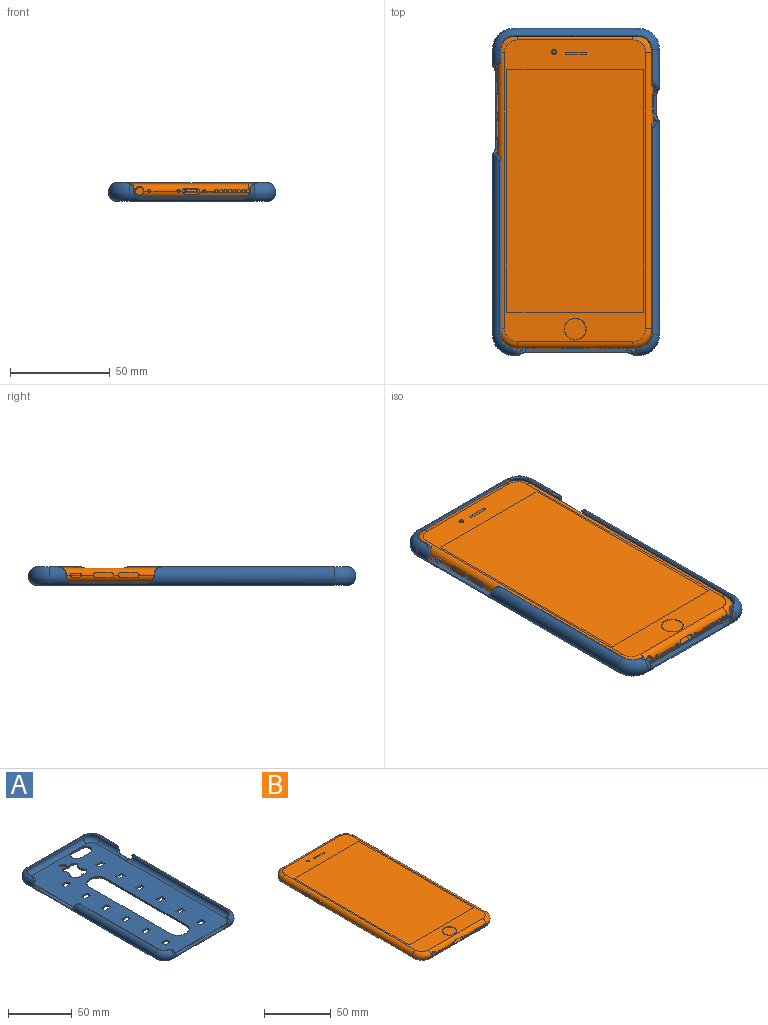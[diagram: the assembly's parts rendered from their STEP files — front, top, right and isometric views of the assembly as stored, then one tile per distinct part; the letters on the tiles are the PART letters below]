
ASSEMBLY  parts=2 mates=1
PART A: 155 faces, bbox 85.4x165.7x9.4 mm
  f0: plane 157.7x77.4mm, normal (0,0,-1), area 9656.5mm2, adj f6,f11,f14,f16,f19,f22,f25,f28
  f1: plane 153.78x73.54mm, normal (0,0,1), area 8760.7mm2, adj f2,f4,f7,f8,f12,f17,f20,f23
  f2: cylinder r=3.5mm len=142.7mm, axis (0,1,0), area 1310mm2, adj f1,f3,f17,f18,f20,f53,f54,f55
  f3: cylinder r=0.5mm len=105.58mm, axis (0,1,0), area 163.5mm2, adj f2,f10,f19,f59,f60
  f4: cylinder r=3.5mm len=142.7mm, axis (0,1,0), area 1033.7mm2, adj f1,f5,f7,f12,f26,f29,f30,f42
  f5: cylinder r=0.5mm len=6.96mm, axis (0,1,0), area 8.5mm2, adj f4,f6,f27,f46,f51
  f6: cylinder r=5mm len=142.7mm, axis (0,1,0), area 1290.4mm2, adj f0,f5,f14,f28,f29,f51,f52,f148
  f7: plane 11.88x0mm, normal (1,0,0), area 0mm2, adj f1,f4,f42
  f8: cylinder r=3.5mm len=62.4mm, axis (1,0,0), area 76.1mm2, adj f1,f9,f12,f15,f17,f31,f33,f34
  f9: cylinder r=0.5mm len=0.88mm, axis (1,0,0), area 0.3mm2, adj f8,f13,f38
  f10: torus R=6.88mm, axis (0,0,1), area 15.2mm2, adj f3,f11,f15,f17,f31,f32
  f11: torus R=5.6mm, axis (0,0,1), area 180.7mm2, adj f0,f10,f16,f19,f32,f140
  f12: torus R=5.74mm, axis (0,0,1), area 129.9mm2, adj f1,f4,f8,f13
  f13: torus R=6.88mm, axis (0,0,1), area 15.2mm2, adj f9,f12,f14,f29,f38,f39
  f14: torus R=5.6mm, axis (0,0,1), area 180.7mm2, adj f0,f6,f13,f16,f39,f132
  f15: cylinder r=0.5mm len=0.88mm, axis (1,0,0), area 0.3mm2, adj f8,f10,f31
  f16: cylinder r=5mm len=62.4mm, axis (1,0,0), area 162.3mm2, adj f0,f11,f14,f133,f134,f135,f136,f137
  f17: torus R=5.74mm, axis (0,0,1), area 129.9mm2, adj f1,f2,f8,f10
  f18: cylinder r=0.5mm len=18.28mm, axis (0,1,0), area 26.3mm2, adj f2,f19,f21,f53,f61
  f19: cylinder r=5mm len=142.7mm, axis (0,1,0), area 1579.2mm2, adj f0,f3,f11,f18,f22,f60,f61,f141
  f20: torus R=5.74mm, axis (0,0,1), area 129.9mm2, adj f1,f2,f21,f23
  f21: torus R=6.88mm, axis (0,0,1), area 16.2mm2, adj f18,f20,f22,f24
  f22: torus R=5.6mm, axis (0,0,1), area 182mm2, adj f0,f19,f21,f25
  f23: cylinder r=3.5mm len=62.4mm, axis (-1,0,0), area 638.1mm2, adj f1,f20,f24,f26
  f24: cylinder r=0.5mm len=62.4mm, axis (-1,0,0), area 98mm2, adj f21,f23,f25,f27
  f25: cylinder r=5mm len=62.4mm, axis (-1,0,0), area 767.6mm2, adj f0,f22,f24,f28
  f26: torus R=5.74mm, axis (0,0,1), area 129.9mm2, adj f1,f4,f23,f27
  f27: torus R=6.88mm, axis (0,0,1), area 16.2mm2, adj f5,f24,f26,f28
  f28: torus R=5.6mm, axis (0,0,1), area 182mm2, adj f0,f6,f25,f27
  f29: cylinder r=0.5mm len=88.94mm, axis (0,1,0), area 137.3mm2, adj f4,f6,f13,f47,f52
  f30: plane 93.82x0mm, normal (1,0,0), area 0.4mm2, adj f1,f4,f43
  f31: cylinder r=3.5mm len=3.87mm, axis (0,1,0), area 8.1mm2, adj f8,f10,f15,f32,f33,f139,f140
  f32: plane 1.41x0.34mm, normal (-1,0,0), area 0.2mm2, adj f10,f11,f31,f140
  f33: plane 1.07x0.54mm, normal (-1,0,0), area 0.5mm2, adj f8,f31,f34,f138
  f34: cylinder r=3.5mm len=4.36mm, axis (0,1,0), area 8.9mm2, adj f8,f33,f35,f137
  f35: plane 50.8x3.01mm, normal (0,0,1), area 152.9mm2, adj f8,f34,f36,f136
  f36: cylinder r=3.5mm len=4.36mm, axis (0,1,0), area 8.9mm2, adj f8,f35,f37,f135
  f37: plane 1.07x0.54mm, normal (1,0,0), area 0.5mm2, adj f8,f36,f38,f134
  f38: cylinder r=3.5mm len=3.87mm, axis (0,1,0), area 8.1mm2, adj f8,f9,f13,f37,f39,f132,f133
  f39: plane 1.41x0.34mm, normal (1,0,0), area 0.2mm2, adj f13,f14,f38,f132
  f40: cylinder r=3.5mm len=0.17mm, axis (0,1,0), area 0mm2, adj f1,f8
  f41: cylinder r=3.5mm len=0.17mm, axis (0,1,0), area 0mm2, adj f1,f8
  f42: cylinder r=3.5mm len=0.17mm, axis (-1,0,0), area 0mm2, adj f1,f4,f7
  f43: cylinder r=3.5mm len=0.17mm, axis (-1,0,0), area 0mm2, adj f1,f4,f30
  f44: plane 37x3.01mm, normal (0,0,1), area 111.4mm2, adj f4,f49,f50,f151
  f45: plane 1.07x0.54mm, normal (0,-1,0), area 0.5mm2, adj f4,f46,f49,f153
  f46: cylinder r=3.5mm len=3.76mm, axis (-1,0,0), area 8.4mm2, adj f4,f5,f45,f51,f154
  f47: cylinder r=3.5mm len=3.76mm, axis (-1,0,0), area 8.4mm2, adj f4,f29,f48,f52,f148
  f48: plane 1.1x1.04mm, normal (0,1,0), area 1.1mm2, adj f4,f47,f50,f149
  f49: cylinder r=3.5mm len=4.36mm, axis (-1,0,0), area 8.9mm2, adj f4,f44,f45,f152
  f50: cylinder r=3.5mm len=4.38mm, axis (-1,0,0), area 10.2mm2, adj f4,f44,f48,f150
  f51: plane 1.37x0.32mm, normal (0,-1,0), area 0.2mm2, adj f5,f6,f46,f154
  f52: plane 1.37x0.32mm, normal (0,1,0), area 0.2mm2, adj f6,f29,f47,f148
  f53: cylinder r=3.5mm len=3.76mm, axis (1,0,0), area 8.4mm2, adj f2,f18,f54,f61,f141
  f54: plane 1.07x0.54mm, normal (0,-1,0), area 0.5mm2, adj f2,f53,f55,f142
  f55: cylinder r=3.5mm len=4.36mm, axis (1,0,0), area 8.9mm2, adj f2,f54,f56,f143
  f56: plane 9x3.01mm, normal (0,0,1), area 27.1mm2, adj f2,f55,f57,f144
  f57: cylinder r=3.5mm len=4.36mm, axis (1,0,0), area 8.9mm2, adj f2,f56,f58,f145
  f58: plane 1.07x0.54mm, normal (0,1,0), area 0.5mm2, adj f2,f57,f59,f146
  f59: cylinder r=3.5mm len=3.76mm, axis (1,0,0), area 8.4mm2, adj f2,f3,f58,f60,f147
  f60: plane 1.37x0.32mm, normal (0,1,0), area 0.2mm2, adj f3,f19,f59,f147
  f61: plane 1.37x0.32mm, normal (0,-1,0), area 0.2mm2, adj f18,f19,f53,f141
  f62: cylinder r=3.5mm len=0.17mm, axis (1,0,0), area 0mm2, adj f1,f2
  f63: cylinder r=3.5mm len=0.17mm, axis (1,0,0), area 0mm2, adj f1,f2
  f64: plane 10.11x1.6mm, normal (0,-1,0), area 16.2mm2, adj f0,f1,f65,f67
  f65: cylinder r=5mm len=10mm, axis (0,0,1), area 25.1mm2, adj f0,f1,f64,f66
  f66: plane 10.11x1.6mm, normal (0,1,0), area 16.2mm2, adj f0,f1,f65,f67
  f67: cylinder r=5mm len=10mm, axis (0,0,1), area 25.1mm2, adj f0,f1,f64,f66
  f68: plane 5.7x1.6mm, normal (0,-1,0), area 9.1mm2, adj f0,f1,f69,f71
  f69: plane 4.7x1.6mm, normal (1,0,0), area 7.5mm2, adj f0,f1,f68,f70
  f70: plane 5.7x1.6mm, normal (0,1,0), area 9.1mm2, adj f0,f1,f69,f71
  f71: plane 4.7x1.6mm, normal (-1,0,0), area 7.5mm2, adj f0,f1,f68,f70
  f72: plane 6.2x1.6mm, normal (0,-1,0), area 9.9mm2, adj f0,f1,f73,f75
  f73: plane 4.2x1.6mm, normal (1,0,0), area 6.7mm2, adj f0,f1,f72,f74
  f74: plane 6.2x1.6mm, normal (0,1,0), area 9.9mm2, adj f0,f1,f73,f75
  f75: plane 4.2x1.6mm, normal (-1,0,0), area 6.7mm2, adj f0,f1,f72,f74
  f76: plane 4.2x1.6mm, normal (1,0,0), area 6.7mm2, adj f0,f1,f77,f79
  f77: plane 6.2x1.6mm, normal (0,1,0), area 9.9mm2, adj f0,f1,f76,f78
  f78: plane 4.2x1.6mm, normal (-1,0,0), area 6.7mm2, adj f0,f1,f77,f79
  f79: plane 6.2x1.6mm, normal (0,-1,0), area 9.9mm2, adj f0,f1,f76,f78
  f80: plane 4.2x1.6mm, normal (-1,0,0), area 6.7mm2, adj f0,f1,f81,f83
  f81: plane 6.2x1.6mm, normal (0,-1,0), area 9.9mm2, adj f0,f1,f80,f82
  f82: plane 4.2x1.6mm, normal (1,0,0), area 6.7mm2, adj f0,f1,f81,f83
  f83: plane 6.2x1.6mm, normal (0,1,0), area 9.9mm2, adj f0,f1,f80,f82
  f84: plane 1.6x1.4mm, normal (0,-1,0), area 2.2mm2, adj f0,f1,f85,f93
  f85: cylinder r=8mm len=8mm, axis (0,0,1), area 20.1mm2, adj f0,f1,f84,f86
  f86: plane 15.56x1.6mm, normal (1,0,0), area 24.9mm2, adj f0,f1,f85,f87
  f87: plane 73.97x1.6mm, normal (1,0,0), area 118.4mm2, adj f0,f1,f86,f88
  f88: cylinder r=8mm len=8mm, axis (0,0,1), area 20.1mm2, adj f0,f1,f87,f89
  f89: plane 1.6x1.4mm, normal (0,1,0), area 2.2mm2, adj f0,f1,f88,f90
  f90: cylinder r=8mm len=8mm, axis (0,0,1), area 20.1mm2, adj f0,f1,f89,f91
  f91: plane 73.97x1.6mm, normal (-1,0,0), area 118.4mm2, adj f0,f1,f90,f92
  f92: plane 15.56x1.6mm, normal (-1,0,0), area 24.9mm2, adj f0,f1,f91,f93
  f93: cylinder r=8mm len=8mm, axis (0,0,1), area 20.1mm2, adj f0,f1,f84,f92
  f94: cylinder r=6.86mm len=10.84mm, axis (0,0,1), area 20.1mm2, adj f0,f1,f95,f97
  f95: extruded ~16.45x2.52mm, area 29.2mm2, adj f0,f1,f94,f96
  f96: extruded ~8.84x3.05mm, area 17.5mm2, adj f0,f1,f95,f97
  f97: extruded ~16.31x5.97mm, area 34.2mm2, adj f0,f1,f94,f96
  f98: extruded ~5.13x4.51mm, area 12.3mm2, adj f0,f1,f99
  f99: extruded ~5.12x4.51mm, area 12mm2, adj f0,f1,f98
  f100: plane 6.2x1.6mm, normal (0,-1,0), area 9.9mm2, adj f0,f1,f101,f103
  f101: plane 4.2x1.6mm, normal (1,0,0), area 6.7mm2, adj f0,f1,f100,f102
  f102: plane 6.2x1.6mm, normal (0,1,0), area 9.9mm2, adj f0,f1,f101,f103
  f103: plane 4.2x1.6mm, normal (-1,0,0), area 6.7mm2, adj f0,f1,f100,f102
  f104: plane 5.7x1.6mm, normal (0,-1,0), area 9.1mm2, adj f0,f1,f105,f107
  f105: plane 4.7x1.6mm, normal (1,0,0), area 7.5mm2, adj f0,f1,f104,f106
  f106: plane 5.7x1.6mm, normal (0,1,0), area 9.1mm2, adj f0,f1,f105,f107
  f107: plane 4.7x1.6mm, normal (-1,0,0), area 7.5mm2, adj f0,f1,f104,f106
  f108: plane 6.2x1.6mm, normal (0,-1,0), area 9.9mm2, adj f0,f1,f109,f111
  f109: plane 4.2x1.6mm, normal (1,0,0), area 6.7mm2, adj f0,f1,f108,f110
  f110: plane 6.2x1.6mm, normal (0,1,0), area 9.9mm2, adj f0,f1,f109,f111
  f111: plane 4.2x1.6mm, normal (-1,0,0), area 6.7mm2, adj f0,f1,f108,f110
  f112: plane 6.2x1.6mm, normal (0,-1,0), area 9.9mm2, adj f0,f1,f113,f115
  f113: plane 4.2x1.6mm, normal (1,0,0), area 6.7mm2, adj f0,f1,f112,f114
  f114: plane 6.2x1.6mm, normal (0,1,0), area 9.9mm2, adj f0,f1,f113,f115
  f115: plane 4.2x1.6mm, normal (-1,0,0), area 6.7mm2, adj f0,f1,f112,f114
  f116: plane 6.2x1.6mm, normal (0,-1,0), area 9.9mm2, adj f0,f1,f117,f119
  f117: plane 4.2x1.6mm, normal (1,0,0), area 6.7mm2, adj f0,f1,f116,f118
  f118: plane 6.2x1.6mm, normal (0,1,0), area 9.9mm2, adj f0,f1,f117,f119
  f119: plane 4.2x1.6mm, normal (-1,0,0), area 6.7mm2, adj f0,f1,f116,f118
  f120: plane 6.2x1.6mm, normal (0,-1,0), area 9.9mm2, adj f0,f1,f121,f123
  f121: plane 4.2x1.6mm, normal (1,0,0), area 6.7mm2, adj f0,f1,f120,f122
  f122: plane 6.2x1.6mm, normal (0,1,0), area 9.9mm2, adj f0,f1,f121,f123
  f123: plane 4.2x1.6mm, normal (-1,0,0), area 6.7mm2, adj f0,f1,f120,f122
  f124: plane 6.2x1.6mm, normal (0,-1,0), area 9.9mm2, adj f0,f1,f125,f127
  f125: plane 4.2x1.6mm, normal (1,0,0), area 6.7mm2, adj f0,f1,f124,f126
  f126: plane 6.2x1.6mm, normal (0,1,0), area 9.9mm2, adj f0,f1,f125,f127
  f127: plane 4.2x1.6mm, normal (-1,0,0), area 6.7mm2, adj f0,f1,f124,f126
  f128: plane 6.2x1.6mm, normal (0,-1,0), area 9.9mm2, adj f0,f1,f129,f131
  f129: plane 4.2x1.6mm, normal (1,0,0), area 6.7mm2, adj f0,f1,f128,f130
  f130: plane 6.2x1.6mm, normal (0,1,0), area 9.9mm2, adj f0,f1,f129,f131
  f131: plane 4.2x1.6mm, normal (-1,0,0), area 6.7mm2, adj f0,f1,f128,f130
  f132: bspline ~1.33x0.67mm, area 0.2mm2, adj f14,f38,f39,f133
  f133: bspline ~3.25x2.39mm, area 1.5mm2, adj f16,f38,f132,f134
  f134: cone r=4.7mm half-angle=45deg, axis (-1,0,0), area 0.2mm2, adj f16,f37,f133,f135
  f135: bspline ~4.04x3.8mm, area 2.9mm2, adj f16,f36,f134,f136
  f136: plane 50.8x0.51mm, normal (0,-0.92,0.38), area 28mm2, adj f16,f35,f135,f137
  f137: bspline ~4.04x3.8mm, area 2.9mm2, adj f16,f34,f136,f138
  f138: cone r=5mm half-angle=45deg, axis (1,0,0), area 0.2mm2, adj f16,f33,f137,f139
  f139: bspline ~3.25x2.39mm, area 1.5mm2, adj f16,f31,f138,f140
  f140: bspline ~1.4x0.68mm, area 0.2mm2, adj f11,f31,f32,f139
  f141: bspline ~3.81x3.54mm, area 1.7mm2, adj f19,f53,f61,f142
  f142: cone r=4.7mm half-angle=45deg, axis (0,1,0), area 0.2mm2, adj f19,f54,f141,f143
  f143: bspline ~4.04x3.8mm, area 2.9mm2, adj f19,f55,f142,f144
  f144: plane 9x0.51mm, normal (0.92,0,0.38), area 5mm2, adj f19,f56,f143,f145
  f145: bspline ~4.04x3.8mm, area 2.9mm2, adj f19,f57,f144,f146
  f146: cone r=4.7mm half-angle=45deg, axis (0,-1,0), area 0.2mm2, adj f19,f58,f145,f147
  f147: bspline ~3.81x3.54mm, area 1.7mm2, adj f19,f59,f60,f146
  f148: bspline ~3.81x3.54mm, area 1.7mm2, adj f6,f47,f52,f149
  f149: cone r=5mm half-angle=45deg, axis (0,-1,0), area 0.5mm2, adj f6,f48,f148,f150
  f150: bspline ~3.76x3.53mm, area 2.7mm2, adj f6,f50,f149,f151
  f151: plane 37x0.51mm, normal (-0.92,0,0.38), area 20.4mm2, adj f6,f44,f150,f152
  f152: bspline ~4.04x3.8mm, area 2.9mm2, adj f6,f49,f151,f153
  f153: cone r=5mm half-angle=45deg, axis (0,1,0), area 0.2mm2, adj f6,f45,f152,f154
  f154: bspline ~3.81x3.54mm, area 1.7mm2, adj f6,f46,f51,f153
PART B: 184 faces, bbox 79.4x159.7x7.8 mm
  f0: cylinder r=3.55mm len=3.55mm, axis (0,1,0), area 12.2mm2, adj f2,f5,f6,f32,f62
  f1: cylinder r=3.55mm len=3.55mm, axis (0,-1,0), area 12.2mm2, adj f2,f4,f7,f36,f59
  f2: plane 70.69x1.5mm, normal (0,0,-1), area 106mm2, adj f0,f1,f8,f39
  f3: cylinder r=3.55mm len=57.79mm, axis (-1,0,0), area 154.9mm2, adj f4,f5,f9,f10,f11,f12,f13,f14
  f4: torus R=6.45mm, axis (0,0,-1), area 41.5mm2, adj f1,f3,f22,f23,f49,f50
  f5: torus R=6.45mm, axis (0,0,-1), area 42.1mm2, adj f0,f3,f24,f25,f69
  f6: cylinder r=3.55mm len=132.83mm, axis (0,1,0), area 710.8mm2, adj f0,f8,f28,f62,f78,f79,f81,f83
  f7: cylinder r=3.55mm len=132.83mm, axis (0,-1,0), area 709.9mm2, adj f1,f8,f27,f59,f74,f99,f100,f101
  f8: plane 132.83x70.69mm, normal (0,0,-1), area 9132.5mm2, adj f2,f6,f7,f26,f48,f65
  f9: cylinder r=3.55mm len=0.95mm, axis (-1,0,0), area 0.1mm2, adj f3,f43,f148
  f10: cylinder r=3.55mm len=2mm, axis (-1,0,0), area 0.4mm2, adj f3,f43,f56,f148
  f11: cylinder r=3.55mm len=13.09mm, axis (-1,0,0), area 4.2mm2, adj f3,f40,f43,f56
  f12: cylinder r=3.55mm len=1.41mm, axis (-1,0,0), area 0.5mm2, adj f3,f40,f43,f109
  f13: cylinder r=3.55mm len=1.49mm, axis (-1,0,0), area 0.7mm2, adj f3,f43,f44,f111
  f14: cylinder r=3.55mm len=5.01mm, axis (-1,0,0), area 2.5mm2, adj f3,f43,f44,f131
  f15: cylinder r=3.55mm len=1.06mm, axis (-1,0,0), area 0.5mm2, adj f3,f43,f129,f131
  f16: cylinder r=3.55mm len=1.09mm, axis (-1,0,0), area 0.5mm2, adj f3,f43,f127,f129
  f17: cylinder r=3.55mm len=1.12mm, axis (-1,0,0), area 0.5mm2, adj f3,f43,f125,f127
  f18: cylinder r=3.55mm len=1.14mm, axis (-1,0,0), area 0.5mm2, adj f3,f43,f123,f125
  f19: cylinder r=3.55mm len=1.17mm, axis (-1,0,0), area 0.5mm2, adj f3,f43,f121,f123
  f20: cylinder r=3.55mm len=1.2mm, axis (-1,0,0), area 0.6mm2, adj f3,f43,f119,f121
  f21: cylinder r=3.55mm len=1.23mm, axis (-1,0,0), area 0.6mm2, adj f3,f43,f117,f119
  f22: torus R=6.45mm, axis (0,0,-1), area 4.3mm2, adj f4,f50
  f23: torus R=6.45mm, axis (0,0,-1), area 5.8mm2, adj f4,f50,f117
  f24: torus R=6.45mm, axis (0,0,-1), area 4.7mm2, adj f5,f72
  f25: torus R=6.45mm, axis (0,0,-1), area 4.7mm2, adj f5,f72
  f26: plane 70.69x1.5mm, normal (0,0,-1), area 106mm2, adj f8,f27,f28,f47
  f27: cylinder r=3.55mm len=3.55mm, axis (0,-1,0), area 12.2mm2, adj f7,f26,f31,f58,f59
  f28: cylinder r=3.55mm len=3.55mm, axis (0,1,0), area 12.1mm2, adj f6,f26,f29,f33,f61,f62
  f29: torus R=6.45mm, axis (0,0,-1), area 42.4mm2, adj f28,f30,f34,f35,f66,f67
  f30: cylinder r=3.55mm len=57.79mm, axis (1,0,0), area 196mm2, adj f29,f31,f68,f70
  f31: torus R=6.45mm, axis (0,0,-1), area 42.1mm2, adj f27,f30,f37,f38,f71
  f32: cylinder r=3.55mm len=2.05mm, axis (0,1,0), area 2.4mm2, adj f0,f39,f69
  f33: cylinder r=3.55mm len=0.28mm, axis (0,1,0), area 0mm2, adj f28,f34,f62
  f34: torus R=6.45mm, axis (0,0,-1), area 3.4mm2, adj f29,f33,f67
  f35: torus R=6.45mm, axis (0,0,-1), area 5.7mm2, adj f29,f67
  f36: cylinder r=3.55mm len=2.05mm, axis (0,-1,0), area 2.4mm2, adj f1,f39,f49
  f37: torus R=6.45mm, axis (0,0,-1), area 4.7mm2, adj f31,f73
  f38: torus R=6.45mm, axis (0,0,-1), area 4.7mm2, adj f31,f73
  f39: plane 70.69x7.57mm, normal (0,0,-1), area 517.3mm2, adj f2,f32,f36,f42,f49,f69
  f40: cylinder r=3.55mm len=1.6mm, axis (-1,0,0), area 0.8mm2, adj f3,f11,f12,f41,f168,f169,f170,f171
  f41: cylinder r=3.55mm len=1.6mm, axis (1,0,0), area 0.9mm2, adj f40,f43,f163,f164,f165,f166,f167,f168
  f42: cylinder r=3.55mm len=57.79mm, axis (-1,0,0), area 124.3mm2, adj f3,f39,f49,f69
  f43: cylinder r=3.55mm len=57.79mm, axis (1,0,0), area 290.7mm2, adj f9,f10,f11,f12,f13,f14,f15,f16
  f44: cylinder r=3.55mm len=1.6mm, axis (-1,0,0), area 0.8mm2, adj f3,f13,f14,f45,f153,f154,f155,f156
  f45: cylinder r=3.55mm len=1.6mm, axis (1,0,0), area 0.9mm2, adj f43,f44,f150,f151,f152,f153,f159,f160
  f46: plane 1.5x1.5mm, normal (0,0,1), area 1mm2, adj f142,f143
  f47: plane 70.69x7.57mm, normal (0,0,-1), area 456.1mm2, adj f26,f58,f61,f66,f68,f71,f104,f144
  f48: plane 18.21x17.51mm, normal (0,0,-1), area 242.8mm2, adj f8
  f49: torus R=6.45mm, axis (0,0,-1), area 24.6mm2, adj f4,f36,f39,f42
  f50: torus R=6.45mm, axis (0,0,-1), area 76.2mm2, adj f4,f22,f23,f43,f59,f63,f117
  f51: cylinder r=1.7mm len=1.7mm, axis (0,0,-1), area 1.5mm2, adj f52,f54,f113
  f52: cylinder r=1.7mm len=6.5mm, axis (1,0,0), area 10.1mm2, adj f51,f53,f54,f114
  f53: cylinder r=1.7mm len=1.7mm, axis (0,0,1), area 1.5mm2, adj f52,f54,f115
  f54: cylinder r=1.7mm len=6.5mm, axis (-1,0,0), area 10.1mm2, adj f51,f52,f53,f116
  f55: plane 8.7x2.95mm, normal (0,-1,0), area 12.7mm2, adj f109,f110,f111,f112,f113,f114,f115,f116
  f56: cylinder r=3.55mm len=1.6mm, axis (-1,0,0), area 1mm2, adj f3,f10,f11,f57
  f57: cylinder r=3.55mm len=1.6mm, axis (1,0,0), area 1mm2, adj f43,f56
  f58: cylinder r=3.55mm len=2.05mm, axis (0,-1,0), area 2.4mm2, adj f27,f47,f71
  f59: cylinder r=3.55mm len=138.07mm, axis (0,1,0), area 739.1mm2, adj f1,f7,f27,f50,f63,f73,f75,f98
  f60: plane 5.61x1.96mm, normal (-1,0,0), area 5.5mm2, adj f88,f89,f90,f91,f92,f93,f94,f95
  f61: cylinder r=3.55mm len=2.09mm, axis (0,1,0), area 2.5mm2, adj f28,f47,f66
  f62: cylinder r=3.55mm len=138.07mm, axis (0,-1,0), area 737.2mm2, adj f0,f6,f28,f33,f63,f67,f72,f79
  f63: plane 150.97x70.69mm, normal (0,0,1), area 2217.1mm2, adj f43,f50,f59,f62,f64,f67,f70,f72
  f64: plane 121.54x68.36mm, normal (0,0,1), area 8308.5mm2, adj f63
  f65: plane 5.18x4.88mm, normal (0,0,-1), area 13.6mm2, adj f8
  f66: torus R=6.45mm, axis (0,0,-1), area 24.8mm2, adj f29,f47,f61,f68
  f67: torus R=6.45mm, axis (0,0,-1), area 76.3mm2, adj f29,f34,f35,f62,f63,f70
  f68: cylinder r=3.55mm len=57.79mm, axis (1,0,0), area 126.3mm2, adj f30,f47,f66,f71,f106
  f69: torus R=6.45mm, axis (0,0,-1), area 24.8mm2, adj f5,f32,f39,f42
  f70: cylinder r=3.55mm len=57.79mm, axis (-1,0,0), area 322.3mm2, adj f30,f63,f67,f73
  f71: torus R=6.45mm, axis (0,0,-1), area 24.8mm2, adj f31,f47,f58,f68
  f72: torus R=6.45mm, axis (0,0,-1), area 76.3mm2, adj f24,f25,f43,f62,f63
  f73: torus R=6.45mm, axis (0,0,-1), area 76.3mm2, adj f37,f38,f59,f63,f70
  f74: cylinder r=3.55mm len=15.81mm, axis (0,-1,0), area 17.2mm2, adj f7,f75,f102
  f75: cylinder r=3.55mm len=15.81mm, axis (0,1,0), area 16.6mm2, adj f59,f74,f102
  f76: cone r=5.45mm half-angle=45deg, axis (0,0,1), area 7.2mm2, adj f63,f77
  f77: plane 10.6x10.6mm, normal (0,0,1), area 88.2mm2, adj f76
  f78: plane 7.4x0.59mm, normal (0,0,-1), area 4.3mm2, adj f6,f79,f81,f82
  f79: cylinder r=1.4mm len=2.8mm, axis (-1,0,0), area 2mm2, adj f6,f62,f78,f80,f82
  f80: plane 7.4x0.59mm, normal (0,0,1), area 4.3mm2, adj f62,f79,f81,f82
  f81: cylinder r=1.4mm len=2.8mm, axis (-1,0,0), area 2mm2, adj f6,f62,f78,f80,f82
  f82: plane 10.2x2.8mm, normal (-1,0,0), area 26.9mm2, adj f78,f79,f80,f81
  f83: plane 7.4x0.59mm, normal (0,0,-1), area 4.3mm2, adj f6,f84,f86,f87
  f84: cylinder r=1.4mm len=2.8mm, axis (-1,0,0), area 2mm2, adj f6,f62,f83,f85,f87
  f85: plane 7.4x0.59mm, normal (0,0,1), area 4.3mm2, adj f62,f84,f86,f87
  f86: cylinder r=1.4mm len=2.8mm, axis (-1,0,0), area 2mm2, adj f6,f62,f83,f85,f87
  f87: plane 10.2x2.8mm, normal (-1,0,0), area 26.9mm2, adj f83,f84,f85,f86
  f88: cylinder r=0.98mm len=1.96mm, axis (-1,0,0), area 1.3mm2, adj f6,f60,f62,f89,f91
  f89: plane 3.65x0.36mm, normal (0,0,-1), area 1.3mm2, adj f60,f62,f88,f90
  f90: cylinder r=0.98mm len=1.96mm, axis (-1,0,0), area 1.3mm2, adj f6,f60,f62,f89,f91
  f91: plane 3.65x0.36mm, normal (0,0,1), area 1.3mm2, adj f6,f60,f88,f90
  f92: cylinder r=0.47mm len=0.93mm, axis (1,0,0), area 1.2mm2, adj f60,f93,f95,f96
  f93: plane 4.31x0.8mm, normal (0,0,-1), area 3.4mm2, adj f60,f92,f94,f96
  f94: cylinder r=0.47mm len=0.93mm, axis (1,0,0), area 1.2mm2, adj f60,f93,f95,f96
  f95: plane 4.31x0.8mm, normal (0,0,1), area 3.4mm2, adj f60,f92,f94,f96
  f96: plane 5.24x0.93mm, normal (-1,0,0), area 4.7mm2, adj f92,f93,f94,f95
  f97: plane 10.2x2.8mm, normal (1,0,0), area 26.9mm2, adj f98,f99,f100,f101
  f98: plane 7.4x0.59mm, normal (0,0,1), area 4.3mm2, adj f59,f97,f99,f101
  f99: cylinder r=1.4mm len=2.8mm, axis (1,0,0), area 2mm2, adj f7,f59,f97,f98,f100
  f100: plane 7.4x0.59mm, normal (0,0,-1), area 4.3mm2, adj f7,f97,f99,f101
  f101: cylinder r=1.4mm len=2.8mm, axis (1,0,0), area 2mm2, adj f7,f59,f97,f98,f100
  f102: cylinder r=1mm len=2mm, axis (1,0,0), area 7.3mm2, adj f74,f75,f103
  f103: plane 2x2mm, normal (1,0,0), area 3.1mm2, adj f102
  f104: cylinder r=3.83mm len=7.66mm, axis (0,0,1), area 16.1mm2, adj f47,f105,f106
  f105: plane 7.66x7.66mm, normal (0,0,-1), area 46.1mm2, adj f104
  f106: plane 2.32x0.18mm, normal (0,0,1), area 0.3mm2, adj f68,f104
  f107: cylinder r=2.02mm len=9.64mm, axis (0,-1,0), area 117.8mm2, adj f108,f148,f149
  f108: plane 4.05x4.05mm, normal (0,-1,0), area 12.9mm2, adj f107
  f109: cylinder r=1.47mm len=5mm, axis (0,-1,0), area 22.5mm2, adj f3,f12,f43,f55,f110,f112
  f110: plane 5.75x4.68mm, normal (0,0,-1), area 26.9mm2, adj f43,f55,f109,f111
  f111: cylinder r=1.47mm len=5mm, axis (0,-1,0), area 22.5mm2, adj f3,f13,f43,f55,f110,f112
  f112: plane 5.75x4.68mm, normal (0,0,1), area 26.9mm2, adj f3,f55,f109,f111
  f113: plane 1.7x0.8mm, normal (1,0,0), area 1.4mm2, adj f51,f55,f114,f116
  f114: plane 6.5x0.8mm, normal (0,0,1), area 5.2mm2, adj f52,f55,f113,f115
  f115: plane 1.7x0.8mm, normal (-1,0,0), area 1.4mm2, adj f53,f55,f114,f116
  f116: plane 6.5x0.8mm, normal (0,0,-1), area 5.2mm2, adj f54,f55,f113,f115
  f117: cylinder r=0.8mm len=1.6mm, axis (0,-1,0), area 4.9mm2, adj f3,f21,f23,f43,f50,f118
  f118: plane 1.6x1.6mm, normal (0,-1,0), area 2mm2, adj f117
  f119: cylinder r=0.8mm len=1.6mm, axis (0,-1,0), area 4.9mm2, adj f3,f20,f21,f43,f120
  f120: plane 1.6x1.6mm, normal (0,-1,0), area 2mm2, adj f119
  f121: cylinder r=0.8mm len=1.6mm, axis (0,-1,0), area 4.9mm2, adj f3,f19,f20,f43,f122
  f122: plane 1.6x1.6mm, normal (0,-1,0), area 2mm2, adj f121
  f123: cylinder r=0.8mm len=1.6mm, axis (0,-1,0), area 4.9mm2, adj f3,f18,f19,f43,f124
  f124: plane 1.6x1.6mm, normal (0,-1,0), area 2mm2, adj f123
  f125: cylinder r=0.8mm len=1.6mm, axis (0,-1,0), area 4.9mm2, adj f3,f17,f18,f43,f126
  f126: plane 1.6x1.6mm, normal (0,-1,0), area 2mm2, adj f125
  f127: cylinder r=0.8mm len=1.6mm, axis (0,-1,0), area 4.9mm2, adj f3,f16,f17,f43,f128
  f128: plane 1.6x1.6mm, normal (0,-1,0), area 2mm2, adj f127
  f129: cylinder r=0.8mm len=1.6mm, axis (0,-1,0), area 4.9mm2, adj f3,f15,f16,f43,f130
  f130: plane 1.6x1.6mm, normal (0,-1,0), area 2mm2, adj f129
  f131: cylinder r=0.8mm len=1.6mm, axis (0,-1,0), area 4.9mm2, adj f3,f14,f15,f43,f132
  f132: plane 1.6x1.6mm, normal (0,-1,0), area 2mm2, adj f131
  f133: cylinder r=0.6mm len=1.2mm, axis (0,0,1), area 0.2mm2, adj f63,f134,f136,f137
  f134: plane 9.5x0.1mm, normal (0,-1,0), area 1mm2, adj f63,f133,f135,f137
  f135: cylinder r=0.6mm len=1.2mm, axis (0,0,1), area 0.2mm2, adj f63,f134,f136,f137
  f136: plane 9.5x0.1mm, normal (0,1,0), area 1mm2, adj f63,f133,f135,f137
  f137: plane 10.7x1.2mm, normal (0,0,1), area 12.5mm2, adj f133,f134,f135,f136
  f138: cylinder r=1.25mm len=2.5mm, axis (0,0,1), area 2mm2, adj f63,f139
  f139: plane 2.5x2.5mm, normal (0,0,1), area 1.8mm2, adj f138,f140
  f140: cylinder r=1mm len=2mm, axis (0,0,1), area 1.6mm2, adj f139,f141
  f141: plane 2x2mm, normal (0,0,1), area 1.4mm2, adj f140,f142
  f142: cylinder r=0.75mm len=1.5mm, axis (0,0,1), area 1.2mm2, adj f46,f141
  f143: sphere r=0.5mm, area 1.6mm2, adj f46
  f144: cylinder r=2.06mm len=4.11mm, axis (0,0,1), area 0.6mm2, adj f47,f145
  f145: plane 4.11x4.11mm, normal (0,0,-1), area 13.3mm2, adj f144
  f146: cylinder r=0.8mm len=1.6mm, axis (0,0,-1), area 0.5mm2, adj f47,f147
  f147: plane 1.6x1.6mm, normal (0,0,-1), area 2mm2, adj f146
  f148: bspline ~4.23x2.35mm, area 2.8mm2, adj f3,f9,f10,f107,f149
  f149: bspline ~4.23x2.35mm, area 2.8mm2, adj f43,f107,f148
  f150: plane 0.2x0.17mm, normal (0,0,-1), area 0mm2, adj f45,f151,f161,f162
  f151: plane 0.35x0.2mm, normal (-1,0,0), area 0.1mm2, adj f45,f150,f152,f162
  f152: plane 0.35x0.2mm, normal (0,0,-1), area 0.1mm2, adj f45,f151,f153,f162
  f153: plane 0.2x0.2mm, normal (-1,0,0), area 0mm2, adj f44,f45,f152,f154,f162
  f154: plane 0.35x0.2mm, normal (0,0,1), area 0.1mm2, adj f44,f153,f155,f162
  f155: plane 0.35x0.2mm, normal (-1,0,0), area 0.1mm2, adj f44,f154,f156,f162
  f156: plane 0.2x0.17mm, normal (0,0,1), area 0mm2, adj f44,f155,f157,f162
  f157: plane 0.35x0.2mm, normal (1,0,0), area 0.1mm2, adj f44,f156,f158,f162
  f158: plane 0.35x0.2mm, normal (0,0,1), area 0.1mm2, adj f44,f157,f159,f162
  f159: plane 0.2x0.2mm, normal (1,0,0), area 0mm2, adj f44,f45,f158,f160,f162
  f160: plane 0.35x0.2mm, normal (0,0,-1), area 0.1mm2, adj f45,f159,f161,f162
  f161: plane 0.35x0.2mm, normal (1,0,0), area 0.1mm2, adj f45,f150,f160,f162
  f162: plane 0.9x0.9mm, normal (0,-1,0), area 0.3mm2, adj f150,f151,f152,f153,f154,f155,f156,f157
  f163: plane 0.35x0.2mm, normal (0,0,-1), area 0.1mm2, adj f41,f164,f174,f175
  f164: plane 0.35x0.2mm, normal (-1,0,0), area 0.1mm2, adj f41,f163,f165,f175
  f165: plane 0.2x0.17mm, normal (0,0,-1), area 0mm2, adj f41,f164,f166,f175
  f166: plane 0.35x0.2mm, normal (1,0,0), area 0.1mm2, adj f41,f165,f167,f175
  f167: plane 0.35x0.2mm, normal (0,0,-1), area 0.1mm2, adj f41,f166,f168,f175
  f168: plane 0.2x0.2mm, normal (1,0,0), area 0mm2, adj f40,f41,f167,f169,f175
  f169: plane 0.35x0.2mm, normal (0,0,1), area 0.1mm2, adj f40,f168,f170,f175
  f170: plane 0.35x0.2mm, normal (1,0,0), area 0.1mm2, adj f40,f169,f171,f175
  f171: plane 0.2x0.17mm, normal (0,0,1), area 0mm2, adj f40,f170,f172,f175
  f172: plane 0.35x0.2mm, normal (-1,0,0), area 0.1mm2, adj f40,f171,f173,f175
  f173: plane 0.35x0.2mm, normal (0,0,1), area 0.1mm2, adj f40,f172,f174,f175
  f174: plane 0.2x0.2mm, normal (-1,0,0), area 0mm2, adj f40,f41,f163,f173,f175
  f175: plane 0.9x0.9mm, normal (0,-1,0), area 0.3mm2, adj f163,f164,f165,f166,f167,f168,f169,f170
  f176: plane 6.9x6.9mm, normal (0,0,1), area 37.4mm2, adj f183
  f177: sphere r=1.52mm, area 4.8mm2, adj f178
  f178: cylinder r=1.12mm len=2.25mm, axis (0,0,-1), area 3.5mm2, adj f177,f179
  f179: plane 2.75x2.75mm, normal (0,0,-1), area 2mm2, adj f178,f180
  f180: plane 3.75x3.75mm, normal (0,0,-1), area 5.1mm2, adj f179,f181
  f181: cylinder r=1.88mm len=3.75mm, axis (0,0,-1), area 11.8mm2, adj f180,f182
  f182: plane 6.9x6.9mm, normal (0,0,-1), area 26.3mm2, adj f181,f183
  f183: cylinder r=3.45mm len=6.9mm, axis (0,0,-1), area 1.1mm2, adj f176,f182
PLACE A rot(axis=(0,0,1),0deg) t=(16.47,42.72,30.55)mm fixed
PLACE B rot(axis=(0,0,1),0deg) t=(16.08,43.34,30.55)mm
MATE slider B.f8 <-> A.f1  axis (0,0,-1) through (16.09,42.2,30.55)mm
